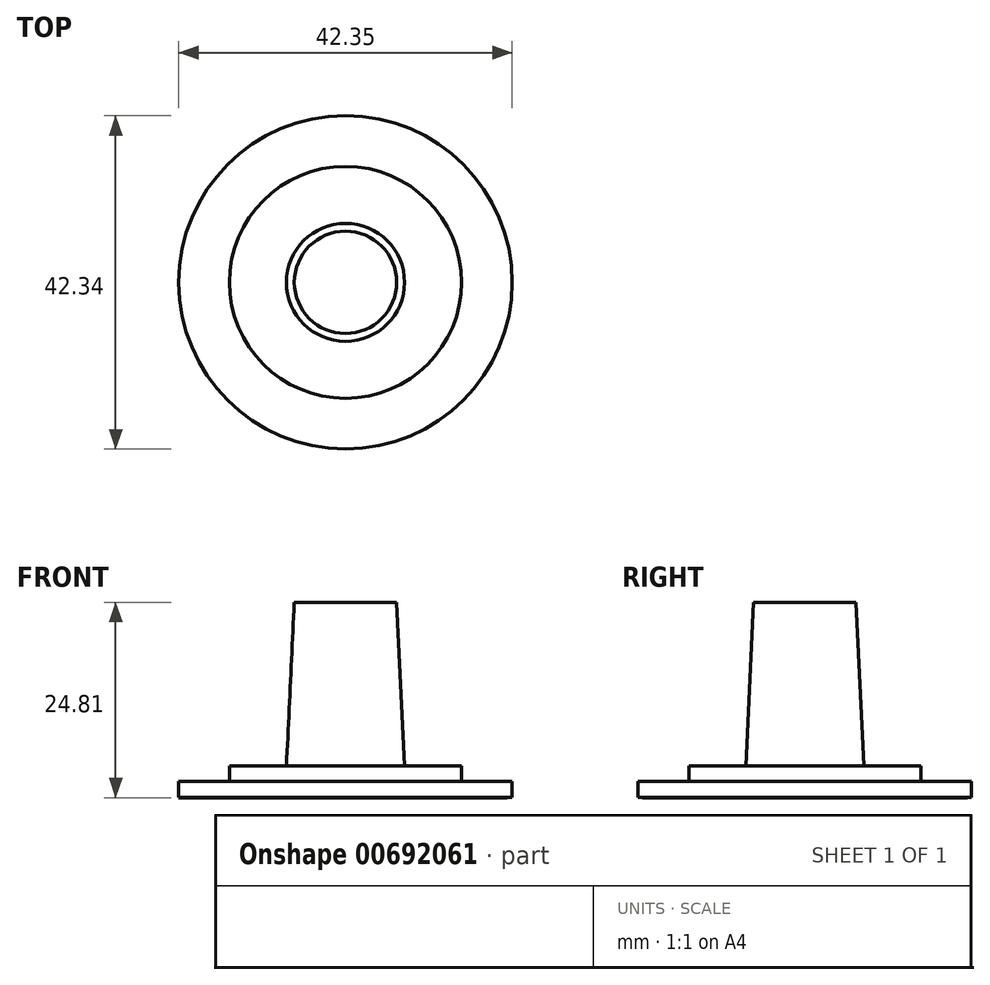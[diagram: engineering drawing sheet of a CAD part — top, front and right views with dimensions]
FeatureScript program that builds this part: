
annotation { "Feature Type Name" : "Feature", "Feature Type Description" : "" }
export const myFeature = defineFeature(function(context is Context, id is Id, definition is map)
    precondition{}
    {
        {
            var Q0;
            Q0=qCreatedBy(makeId("Front.planeOp"),FACE);
            var sketch = newSketch(context, id + "F0", { "sketchPlane" : qUnion([Q0])});
            skLineSegment(sketch, "E0", {"start": v(-53.69, 16.84) * mm, "end": v(-53.69, 18.84) * mm});
            skLineSegment(sketch, "E1", {"start": v(-53.69, 18.84) * mm, "end": v(-47.25, 18.84) * mm});
            skLineSegment(sketch, "E2", {"start": v(-47.25, 18.84) * mm, "end": v(-47.25, 20.84) * mm});
            skLineSegment(sketch, "E3", {"start": v(-47.25, 20.84) * mm, "end": v(-40.01, 20.84) * mm});
            skLineSegment(sketch, "E4", {"start": v(-40.01, 20.84) * mm, "end": v(-39.01, 41.59) * mm});
            skLineSegment(sketch, "E5", {"start": v(-39.01, 41.59) * mm, "end": v(-32.51, 41.59) * mm});
            skLineSegment(sketch, "E6", {"start": v(-32.51, 41.59) * mm, "end": v(-32.51, 16.78) * mm});
            skLineSegment(sketch, "E7", {"start": v(-32.51, 16.78) * mm, "end": v(-53.69, 16.78) * mm});
            skSolve(sketch);
        }
        {
            var Q0;
            Q0=sQuery(id+"F0.wireOp",EDGE,"E0");
            var Q1;
            Q1=sQuery(id+"F0.wireOp",EDGE,"E1");
            var Q2;
            Q2=sQuery(id+"F0.wireOp",EDGE,"E2");
            var Q3;
            Q3=sQuery(id+"F0.wireOp",EDGE,"E3");
            var Q4;
            Q4=sQuery(id+"F0.wireOp",EDGE,"E4");
            var Q5;
            Q5=sQuery(id+"F0.wireOp",EDGE,"E5");
            var Q6;
            Q6=sQuery(id+"F0.wireOp",EDGE,"E7");
            var Q7;
            Q7=sQuery(id+"F0.wireOp",EDGE,"E6");
            revolve(context, id + "F1", {"bodyType" : ToolBodyType.SURFACE, "surfaceEntities" : qUnion([Q0, Q1, Q2, Q3, Q4, Q5, Q6]), "axis" : qUnion([Q7]), "revolveType" : RevolveType.FULL});
        }
    });
